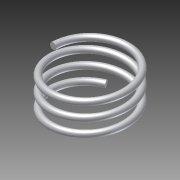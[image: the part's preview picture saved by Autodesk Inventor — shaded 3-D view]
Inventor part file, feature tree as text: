
AUTODESK INVENTOR PART (.ipt)
format: ipt  version: 2012 (Build 160160000, 160)  size: 299,520 bytes
history: native  units: in
note: dims shown in document units (in); Inventor stores cm internally (conversion verified against a paired STEP export)
features: helix x1, sketch x1
ambient origin geometry x8: Origin, YZ Plane, XZ Plane, XY Plane, X Axis, Y Axis, Z Axis, Center Point
bodies: Solid1 (feature_tree)
feature tree (2):
  helix  "Coil1"  [1 undecoded]
  sketch  "Sketch1"  dims[d1=0.6625in d2=0.25in d3=0.7in d4=0.3937in d5=0.0in d6=90.0deg d7=90.0deg d8=0.0in d9=0.0in]
note: 1 required parameter value undecoded (feature->parameter linkage not recoverable at this tier; creation-order binding heuristic only, values carry confidence <= 0.55)
